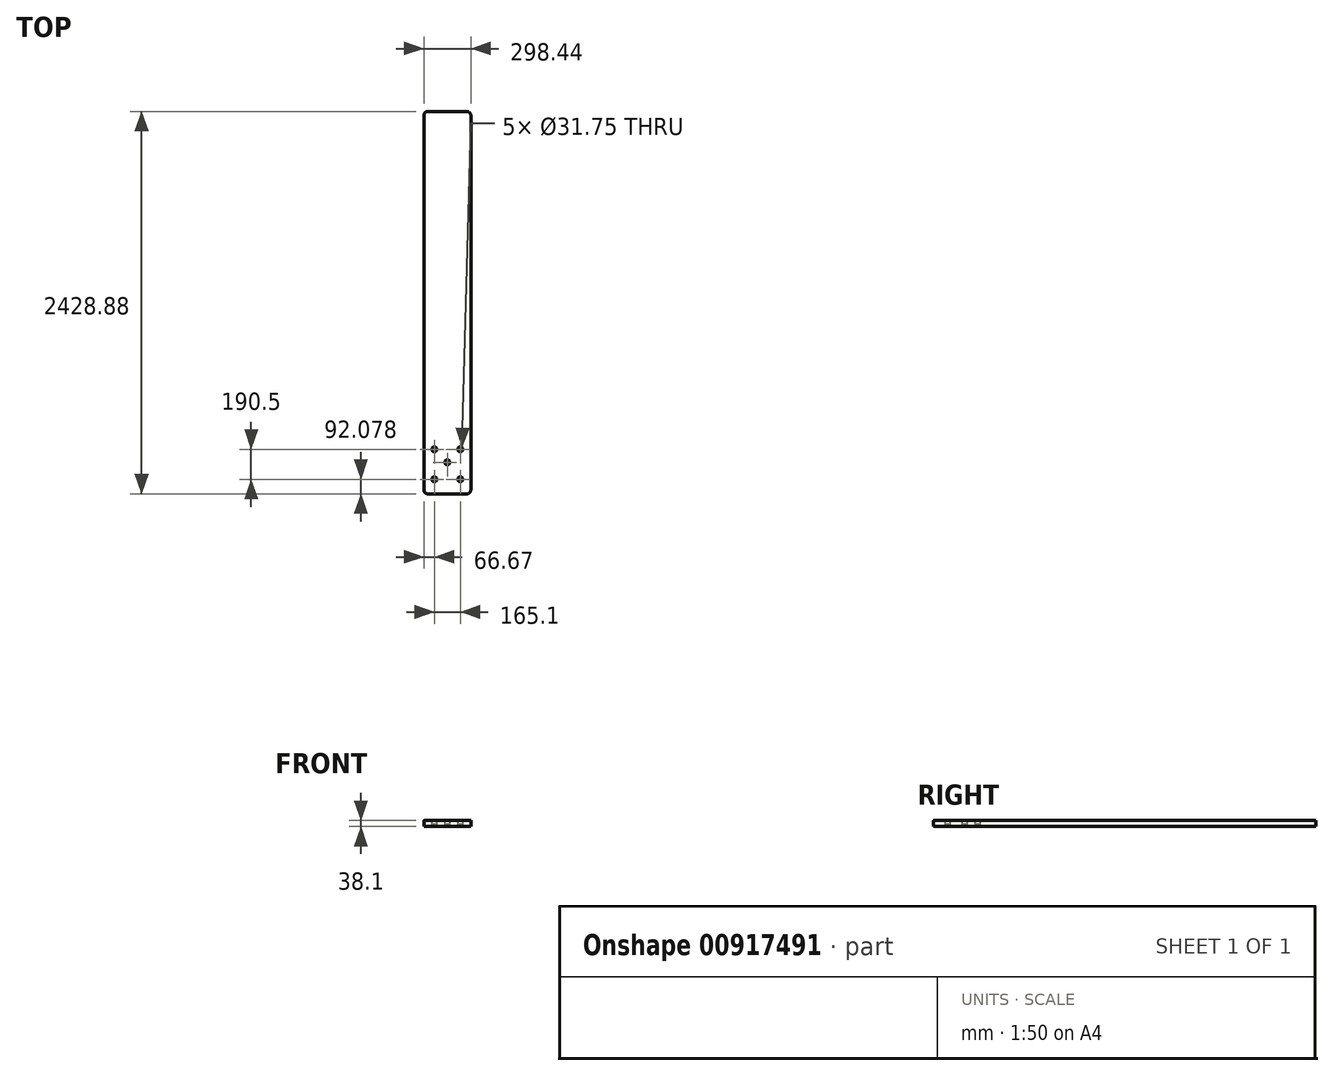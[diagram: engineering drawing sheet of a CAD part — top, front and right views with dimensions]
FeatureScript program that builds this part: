
annotation { "Feature Type Name" : "Feature", "Feature Type Description" : "" }
export const myFeature = defineFeature(function(context is Context, id is Id, definition is map)
    precondition{}
    {
        {
            var Q0;
            Q0=qCreatedBy(makeId("Top.planeOp"),FACE);
            var sketch = newSketch(context, id + "F0", { "sketchPlane" : qUnion([Q0])});
            skLineSegment(sketch, "E0.bottom", {"start": v(149.22, 1214.44) * mm, "end": v(-149.23, 1214.44) * mm});
            skLineSegment(sketch, "E0.top", {"start": v(149.23, -1214.44) * mm, "end": v(-149.22, -1214.44) * mm});
            skLineSegment(sketch, "E0.left", {"start": v(149.22, 1214.44) * mm, "end": v(149.23, -1214.44) * mm});
            skLineSegment(sketch, "E0.right", {"start": v(-149.23, 1214.44) * mm, "end": v(-149.22, -1214.44) * mm});
            skPoint(sketch, "E0.middle", {"position": v(0, 0) * mm});
            skSolve(sketch);
        }
        {
            var Q0;
            Q0=qSketchRegion(id+"F0",true);
            extrude(context, id + "F1", {"entities" : qUnion([Q0]), "depth" : 38.1 * mm, "offsetDistance" : 25.4 * mm});
        }
        {
            var Q0;
            Q0=makeQuery(id+"F1.opExtrude","SWEPT_EDGE",EDGE,{"disambiguationData":[OSD([sQuery(id+"F0.wireOp",EDGE,"E0.bottom"),sQuery(id+"F0.wireOp",EDGE,"E0.left")])]});
            fillet(context, id + "F2", {"entities" : qUnion([Q0]), "radius" : 25.4 * mm, "tangentPropagation" : true, "allowEdgeOverflow" : false});
        }
        {
            var Q0;
            Q0=makeQuery(id+"F1.opExtrude","SWEPT_EDGE",EDGE,{"disambiguationData":[OSD([sQuery(id+"F0.wireOp",EDGE,"E0.bottom"),sQuery(id+"F0.wireOp",EDGE,"E0.right")])]});
            fillet(context, id + "F3", {"entities" : qUnion([Q0]), "radius" : 25.4 * mm, "tangentPropagation" : true, "allowEdgeOverflow" : false});
        }
        {
            var Q0;
            Q0=makeQuery(id+"F1.opExtrude","SWEPT_EDGE",EDGE,{"disambiguationData":[OSD([sQuery(id+"F0.wireOp",EDGE,"E0.top"),sQuery(id+"F0.wireOp",EDGE,"E0.right")])]});
            var Q1;
            Q1=makeQuery(id+"F1.opExtrude","SWEPT_EDGE",EDGE,{"disambiguationData":[OSD([sQuery(id+"F0.wireOp",EDGE,"E0.top"),sQuery(id+"F0.wireOp",EDGE,"E0.left")])]});
            fillet(context, id + "F4", {"entities" : qUnion([Q0, Q1]), "radius" : 25.4 * mm, "tangentPropagation" : true, "allowEdgeOverflow" : false});
        }
        {
            var Q0;
            Q0=makeQuery(id+"F1.opExtrude","CAP_FACE",FACE,{"disambiguationData":[OSD([sQuery(id+"F0.wireOp",EDGE,"E0.bottom"),sQuery(id+"F0.wireOp",EDGE,"E0.top"),sQuery(id+"F0.wireOp",EDGE,"E0.left"),sQuery(id+"F0.wireOp",EDGE,"E0.right")])],"isStart":false});
            var sketch = newSketch(context, id + "F5", { "sketchPlane" : qUnion([Q0])});
            skCircle(sketch, "E1", {"center": v(-82.55, -1122.36) * mm, "radius": 15.88 * mm});
            skCircle(sketch, "E2", {"center": v(82.55, -1122.36) * mm, "radius": 15.88 * mm});
            skCircle(sketch, "E3", {"center": v(0, -1014.41) * mm, "radius": 15.88 * mm});
            skCircle(sketch, "E4", {"center": v(-82.55, -931.86) * mm, "radius": 15.88 * mm});
            skCircle(sketch, "E5", {"center": v(82.55, -931.86) * mm, "radius": 15.88 * mm});
            skSolve(sketch);
        }
        {
            var Q0;
            Q0=sQuery(id+"F5.wireOp",VERTEX,"E1.center");
            var Q1;
            Q1=sQuery(id+"F5.wireOp",VERTEX,"E2.center");
            var Q2;
            Q2=sQuery(id+"F5.wireOp",VERTEX,"E3.center");
            var Q3;
            Q3=sQuery(id+"F5.wireOp",VERTEX,"E5.center");
            var Q4;
            Q4=sQuery(id+"F5.wireOp",VERTEX,"E4.center");
            var Q5;
            Q5=makeQuery(id+"F1.opExtrude","SWEPT_BODY",BODY,{"disambiguationData":[OSD([sQuery(id+"F0.wireOp",EDGE,"E0.bottom"),sQuery(id+"F0.wireOp",EDGE,"E0.top"),sQuery(id+"F0.wireOp",EDGE,"E0.left"),sQuery(id+"F0.wireOp",EDGE,"E0.right")])]});
            hole(context, id + "F6", {"style" : HoleStyle.SIMPLE, "endStyle" : HoleEndStyle.BLIND, "holeDiameter" : 31.75 * mm, "majorDiameter" : 6.35 * mm, "holeDepth" : 25.4 * mm, "isTappedThrough" : true, "tappedDepth" : 12.7 * mm, "tapClearance" : 3, "locations" : qUnion([Q0, Q1, Q2, Q3, Q4]), "scope" : qUnion([Q5])});
        }
    });
